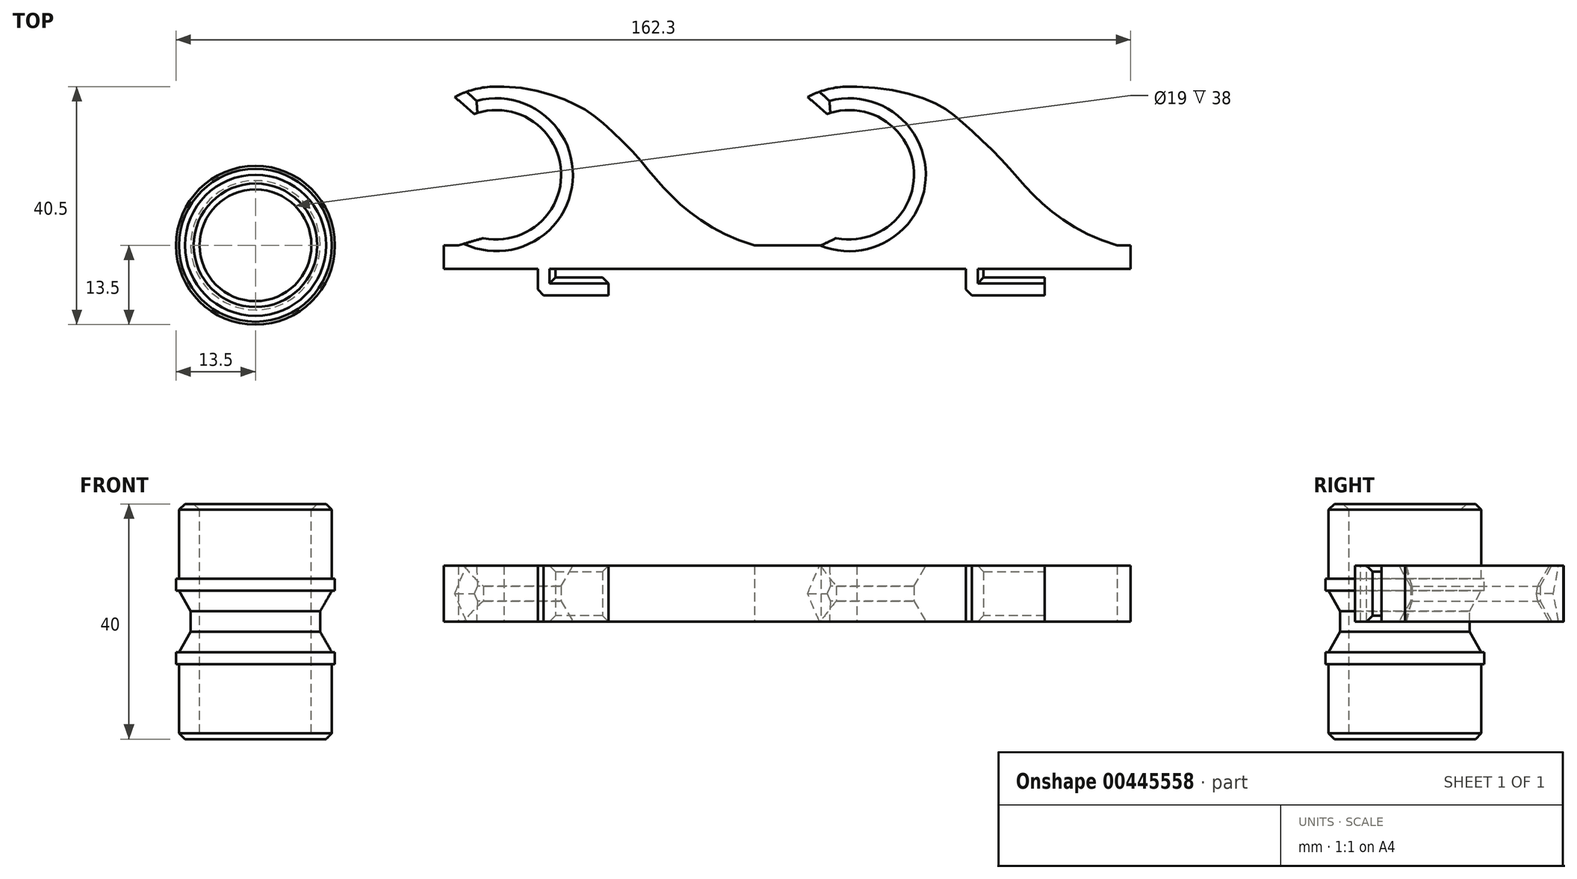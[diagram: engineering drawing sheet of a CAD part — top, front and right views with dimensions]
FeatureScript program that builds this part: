
annotation { "Feature Type Name" : "Feature", "Feature Type Description" : "" }
export const myFeature = defineFeature(function(context is Context, id is Id, definition is map)
    precondition{}
    {
        {
            var Q0;
            Q0=qCreatedBy(makeId("Top.planeOp"),FACE);
            var sketch = newSketch(context, id + "F0", { "sketchPlane" : qUnion([Q0])});
            skLineSegment(sketch, "E0", {"start": v(0, 0) * mm, "end": v(60.8, 0) * mm});
            skLineSegment(sketch, "E1", {"start": v(0, 0) * mm, "end": v(-12, 0) * mm});
            skLineSegment(sketch, "E2", {"start": v(-12, -4) * mm, "end": v(-12, -8.5) * mm});
            skLineSegment(sketch, "E3", {"start": v(-12, -8.5) * mm, "end": v(0, -8.5) * mm});
            skLineSegment(sketch, "E4", {"start": v(0, -8.5) * mm, "end": v(0, -5.5) * mm});
            skLineSegment(sketch, "E5", {"start": v(0, -5.5) * mm, "end": v(-9, -5.5) * mm});
            skLineSegment(sketch, "E6", {"start": v(-9, -5.5) * mm, "end": v(-9, -4) * mm});
            skLineSegment(sketch, "E7", {"start": v(-9, -4) * mm, "end": v(0, -4) * mm});
            skLineSegment(sketch, "E8", {"start": v(60.8, -4) * mm, "end": v(60.8, -8.5) * mm});
            skLineSegment(sketch, "E9", {"start": v(60.8, -8.5) * mm, "end": v(74.2, -8.5) * mm});
            skLineSegment(sketch, "E10", {"start": v(74.2, -8.5) * mm, "end": v(74.2, -5.5) * mm});
            skLineSegment(sketch, "E11", {"start": v(74.2, -5.5) * mm, "end": v(63.8, -5.5) * mm});
            skLineSegment(sketch, "E12", {"start": v(63.8, -5.5) * mm, "end": v(63.8, -4) * mm});
            skLineSegment(sketch, "E13", {"start": v(63.8, -4) * mm, "end": v(74.2, -4) * mm});
            skLineSegment(sketch, "E14", {"start": v(72.8, 0) * mm, "end": v(60.8, 0) * mm});
            skLineSegment(sketch, "E15", {"start": v(-12, 0) * mm, "end": v(-28, 0) * mm});
            skLineSegment(sketch, "E16", {"start": v(88.8, 0) * mm, "end": v(72.8, 0) * mm});
            skLineSegment(sketch, "E17", {"start": v(-28, 0) * mm, "end": v(-28, -4) * mm});
            skLineSegment(sketch, "E18", {"start": v(-28, -4) * mm, "end": v(-12, -4) * mm});
            skLineSegment(sketch, "E19", {"start": v(88.8, 0) * mm, "end": v(88.8, -4) * mm});
            skLineSegment(sketch, "E20", {"start": v(88.8, -4) * mm, "end": v(74.2, -4) * mm});
            skLineSegment(sketch, "E21", {"start": v(0, -4) * mm, "end": v(60.8, -4) * mm});
            skLineSegment(sketch, "E22", {"start": v(24.4, 0) * mm, "end": v(24.4, -4) * mm});
            skSolve(sketch);
        }
        {
            var Q0;
            Q0=qSketchRegion(id+"F0",true);
            extrude(context, id + "F1", {"entities" : qUnion([Q0]), "depth" : 9.5 * mm});
        }
        {
            var Q0;
            Q0=makeQuery(id+"F1.opExtrude","SWEPT_EDGE",EDGE,{"disambiguationData":[OSD([sQuery(id+"F0.wireOp",EDGE,"E2"),sQuery(id+"F0.wireOp",EDGE,"E3")])]});
            var Q1;
            Q1=makeQuery(id+"F1.opExtrude","SWEPT_EDGE",EDGE,{"disambiguationData":[OSD([sQuery(id+"F0.wireOp",EDGE,"E8"),sQuery(id+"F0.wireOp",EDGE,"E9")])]});
            var Q2;
            Q2=makeQuery(id+"F1.opExtrude","SWEPT_EDGE",EDGE,{"disambiguationData":[OSD([sQuery(id+"F0.wireOp",EDGE,"E4"),sQuery(id+"F0.wireOp",EDGE,"E5")])]});
            var Q3;
            Q3=makeQuery(id+"F1.opExtrude","CAP_EDGE",EDGE,{"disambiguationData":[OSD([sQuery(id+"F0.wireOp",EDGE,"E11")])],"isStart":true});
            var Q4;
            Q4=makeQuery(id+"F1.opExtrude","CAP_EDGE",EDGE,{"disambiguationData":[OSD([sQuery(id+"F0.wireOp",EDGE,"E5")])],"isStart":true});
            var Q5;
            Q5=makeQuery(id+"F1.opExtrude","CAP_EDGE",EDGE,{"disambiguationData":[OSD([sQuery(id+"F0.wireOp",EDGE,"E6")])],"isStart":true});
            var Q6;
            Q6=makeQuery(id+"F1.opExtrude","CAP_EDGE",EDGE,{"disambiguationData":[OSD([sQuery(id+"F0.wireOp",EDGE,"E12")])],"isStart":true});
            var Q7;
            Q7=makeQuery(id+"F1.opExtrude","CAP_EDGE",EDGE,{"disambiguationData":[OSD([sQuery(id+"F0.wireOp",EDGE,"E11")])],"isStart":false});
            var Q8;
            Q8=makeQuery(id+"F1.opExtrude","CAP_EDGE",EDGE,{"disambiguationData":[OSD([sQuery(id+"F0.wireOp",EDGE,"E12")])],"isStart":false});
            var Q9;
            Q9=makeQuery(id+"F1.opExtrude","CAP_EDGE",EDGE,{"disambiguationData":[OSD([sQuery(id+"F0.wireOp",EDGE,"E5")])],"isStart":false});
            var Q10;
            Q10=makeQuery(id+"F1.opExtrude","CAP_EDGE",EDGE,{"disambiguationData":[OSD([sQuery(id+"F0.wireOp",EDGE,"E6")])],"isStart":false});
            chamfer(context, id + "F2", {"entities" : qUnion([Q0, Q1, Q2, Q3, Q4, Q5, Q6, Q7, Q8, Q9, Q10]), "width" : 1 * mm, "tangentPropagation" : true});
        }
        {
            var Q0;
            Q0=qCreatedBy(makeId("Top.planeOp"),FACE);
            var sketch = newSketch(context, id + "F3", { "sketchPlane" : qUnion([Q0])});
            skArc(sketch, "E23", {"start": v(38.77, 1.22) * mm, "mid": v(51.01, 16.5) * mm, "end": v(31.47, 17.55) * mm});
            skArc(sketch, "E24", {"start": v(42.27, 26.94) * mm, "mid": v(36.55, 26.33) * mm, "end": v(31.47, 23.6) * mm});
            skLineSegment(sketch, "E25", {"start": v(31.47, 17.55) * mm, "end": v(31.47, 23.6) * mm});
            skLineSegment(sketch, "E26", {"start": v(38.77, 1.22) * mm, "end": v(38.77, 0) * mm});
            skLineSegment(sketch, "E27", {"start": v(38.77, 0) * mm, "end": v(86.52, 0) * mm});
            skLineSegment(sketch, "E28", {"start": v(38.77, 1.22) * mm, "end": v(36.18, 0) * mm});
            skLineSegment(sketch, "E29", {"start": v(36.18, 0) * mm, "end": v(38.77, 0) * mm});
            skFitSpline(sketch, "E30", {"points": [v(42.27, 26.94) * mm, v(55.04, 24.44) * mm, v(60.1, 20.96) * mm, v(66.27, 15.18) * mm, v(71.09, 9.79) * mm, v(76.79, 4.7) * mm, v(86.52, 0) * mm], "startDerivative": vector(69.14, -0.33) * mm, "endDerivative": vector(63.43, -17.78) * mm});
            skArc(sketch, "E31", {"start": v(-21.23, 1.22) * mm, "mid": v(-8.99, 16.5) * mm, "end": v(-28.53, 17.55) * mm});
            skArc(sketch, "E32", {"start": v(-17.73, 26.94) * mm, "mid": v(-23.45, 26.33) * mm, "end": v(-28.53, 23.6) * mm});
            skLineSegment(sketch, "E33", {"start": v(-28.53, 17.55) * mm, "end": v(-28.53, 23.6) * mm});
            skLineSegment(sketch, "E34", {"start": v(-21.23, 1.22) * mm, "end": v(-21.23, 0) * mm});
            skLineSegment(sketch, "E35", {"start": v(-21.23, 0) * mm, "end": v(24.84, 0) * mm});
            skLineSegment(sketch, "E36", {"start": v(-21.23, 1.22) * mm, "end": v(-25.5, 0) * mm});
            skLineSegment(sketch, "E37", {"start": v(-25.5, 0) * mm, "end": v(-21.23, 0) * mm});
            skFitSpline(sketch, "E38", {"points": [v(-17.73, 26.94) * mm, v(-6.64, 24.44) * mm, v(-1.42, 21.22) * mm, v(5.01, 14.92) * mm, v(9.4, 9.79) * mm, v(15.1, 4.7) * mm, v(24.84, 0) * mm], "startDerivative": vector(68.3, -0.33) * mm, "endDerivative": vector(63.43, -17.78) * mm});
            skSolve(sketch);
        }
        {
            var Q0;
            Q0=qSketchRegion(id+"F3",true);
            extrude(context, id + "F4", {"entities" : qUnion([Q0]), "operationType" : NewBodyOperationType.ADD, "depth" : 9.5 * mm});
        }
        {
            var Q0;
            Q0=makeQuery(id+"F4.opExtrude","CAP_EDGE",EDGE,{"disambiguationData":[OSD([sQuery(id+"F3.wireOp",EDGE,"E23")])],"isStart":false});
            var Q1;
            Q1=makeQuery(id+"F4.opExtrude","CAP_EDGE",EDGE,{"disambiguationData":[OSD([sQuery(id+"F3.wireOp",EDGE,"E31")])],"isStart":false});
            chamfer(context, id + "F5", {"entities" : qUnion([Q0, Q1]), "chamferType" : ChamferType.TWO_OFFSETS, "width1" : 3.5 * mm, "oppositeDirection" : false, "width2" : 2 * mm, "tangentPropagation" : true});
        }
        {
            var Q0;
            Q0=makeQuery(id+"F4.opExtrude","CAP_EDGE",EDGE,{"disambiguationData":[OSD([sQuery(id+"F3.wireOp",EDGE,"E31")])],"isStart":true});
            var Q1;
            Q1=makeQuery(id+"F4.opExtrude","CAP_EDGE",EDGE,{"disambiguationData":[OSD([sQuery(id+"F3.wireOp",EDGE,"E23")])],"isStart":true});
            chamfer(context, id + "F6", {"entities" : qUnion([Q0, Q1]), "chamferType" : ChamferType.TWO_OFFSETS, "width1" : 2 * mm, "oppositeDirection" : false, "width2" : 3.5 * mm, "tangentPropagation" : true});
        }
        {
            var Q0;
            Q0=makeQuery(id+"F5.opChamfer","BLEND_EDGE",EDGE,{"blendedFrom":[makeQuery(id+"F4.opExtrude","CAP_EDGE",EDGE,{"disambiguationData":[OSD([sQuery(id+"F3.wireOp",EDGE,"E23")])],"isStart":false}),makeQuery(id+"F4.opExtrude","SWEPT_FACE",FACE,{"disambiguationData":[OSD([sQuery(id+"F3.wireOp",EDGE,"E25")])]})],"blendedInto":[makeQuery(id+"F4.opExtrude","SWEPT_FACE",FACE,{"disambiguationData":[OSD([sQuery(id+"F3.wireOp",EDGE,"E25")])]})]});
            var Q1;
            Q1=makeQuery(id+"F6.opChamfer","BLEND_EDGE",EDGE,{"blendedFrom":[makeQuery(id+"F4.opExtrude","CAP_EDGE",EDGE,{"disambiguationData":[OSD([sQuery(id+"F3.wireOp",EDGE,"E23")])],"isStart":true}),makeQuery(id+"F4.opExtrude","SWEPT_FACE",FACE,{"disambiguationData":[OSD([sQuery(id+"F3.wireOp",EDGE,"E25")])]})],"blendedInto":[makeQuery(id+"F4.opExtrude","SWEPT_FACE",FACE,{"disambiguationData":[OSD([sQuery(id+"F3.wireOp",EDGE,"E25")])]})]});
            var Q2;
            Q2=makeQuery(id+"F5.opChamfer","BLEND_EDGE",EDGE,{"blendedFrom":[makeQuery(id+"F4.opExtrude","CAP_EDGE",EDGE,{"disambiguationData":[OSD([sQuery(id+"F3.wireOp",EDGE,"E31")])],"isStart":false}),makeQuery(id+"F4.opExtrude","SWEPT_FACE",FACE,{"disambiguationData":[OSD([sQuery(id+"F3.wireOp",EDGE,"E33")])]})],"blendedInto":[makeQuery(id+"F4.opExtrude","SWEPT_FACE",FACE,{"disambiguationData":[OSD([sQuery(id+"F3.wireOp",EDGE,"E33")])]})]});
            var Q3;
            Q3=makeQuery(id+"F6.opChamfer","BLEND_EDGE",EDGE,{"blendedFrom":[makeQuery(id+"F4.opExtrude","CAP_EDGE",EDGE,{"disambiguationData":[OSD([sQuery(id+"F3.wireOp",EDGE,"E31")])],"isStart":true}),makeQuery(id+"F4.opExtrude","SWEPT_FACE",FACE,{"disambiguationData":[OSD([sQuery(id+"F3.wireOp",EDGE,"E33")])]})],"blendedInto":[makeQuery(id+"F4.opExtrude","SWEPT_FACE",FACE,{"disambiguationData":[OSD([sQuery(id+"F3.wireOp",EDGE,"E33")])]})]});
            chamfer(context, id + "F7", {"entities" : qUnion([Q0, Q1, Q2, Q3]), "width" : 5 * mm, "tangentPropagation" : true});
        }
        {
            var Q0;
            Q0=qCreatedBy(makeId("Front.planeOp"),FACE);
            var sketch = newSketch(context, id + "F8", { "sketchPlane" : qUnion([Q0])});
            skLineSegment(sketch, "E39", {"start": v(0, 0) * mm, "end": v(-60, 0) * mm});
            skLineSegment(sketch, "E40", {"start": v(-60, 0) * mm, "end": v(-60, -12.67) * mm});
            skLineSegment(sketch, "E41", {"start": v(-60, 0) * mm, "end": v(-69.5, 0) * mm});
            skLineSegment(sketch, "E42", {"start": v(-69.5, 0) * mm, "end": v(-73, 0) * mm});
            skLineSegment(sketch, "E43", {"start": v(-69.5, 0) * mm, "end": v(-69.5, 20) * mm});
            skLineSegment(sketch, "E44", {"start": v(-69.5, 20) * mm, "end": v(-73, 20) * mm});
            skLineSegment(sketch, "E45", {"start": v(-73, 20) * mm, "end": v(-73, 5.25) * mm});
            skLineSegment(sketch, "E46", {"start": v(-73, 5.25) * mm, "end": v(-71, 1.75) * mm});
            skLineSegment(sketch, "E47", {"start": v(-71, 1.75) * mm, "end": v(-71, 0) * mm});
            skLineSegment(sketch, "E48.MirrorCS", {"start": v(-71, -1.75) * mm, "end": v(-71, 0) * mm});
            skLineSegment(sketch, "E49.MirrorCS", {"start": v(-73, -5.25) * mm, "end": v(-71, -1.75) * mm});
            skLineSegment(sketch, "E50.MirrorCS", {"start": v(-73, -20) * mm, "end": v(-73, -5.25) * mm});
            skLineSegment(sketch, "E51.MirrorCS", {"start": v(-69.5, -20) * mm, "end": v(-73, -20) * mm});
            skLineSegment(sketch, "E52.MirrorCS", {"start": v(-69.5, 0) * mm, "end": v(-69.5, -20) * mm});
            skLineSegment(sketch, "E53", {"start": v(-73, 5.25) * mm, "end": v(-73.5, 5.25) * mm});
            skLineSegment(sketch, "E54", {"start": v(-73.5, 5.25) * mm, "end": v(-73.5, 7.25) * mm});
            skLineSegment(sketch, "E55", {"start": v(-73.5, 7.25) * mm, "end": v(-73, 7.25) * mm});
            skLineSegment(sketch, "E56.MirrorCS", {"start": v(-73.5, -7.25) * mm, "end": v(-73, -7.25) * mm});
            skLineSegment(sketch, "E57.MirrorCS", {"start": v(-73.5, -5.25) * mm, "end": v(-73.5, -7.25) * mm});
            skLineSegment(sketch, "E58.MirrorCS", {"start": v(-73, -5.25) * mm, "end": v(-73.5, -5.25) * mm});
            skSolve(sketch);
        }
        {
            var Q0;
            Q0=qSketchRegion(id+"F8",true);
            var Q1;
            Q1=sQuery(id+"F8.wireOp",EDGE,"E40");
            revolve(context, id + "F9", {"entities" : qUnion([Q0]), "axis" : qUnion([Q1]), "revolveType" : RevolveType.FULL});
        }
        {
            var Q0;
            Q0=makeQuery(id+"F9.opRevolve","SWEPT_FACE",FACE,{"disambiguationData":[OSD([sQuery(id+"F8.wireOp",EDGE,"E51.MirrorCS")])]});
            var sketch = newSketch(context, id + "F10", { "sketchPlane" : qUnion([Q0])});
            skCircle(sketch, "E59", {"center": v(-60, 0) * mm, "radius": 13 * mm});
            skSolve(sketch);
        }
        {
            var Q0;
            Q0=qSketchRegion(id+"F10",true);
            extrude(context, id + "F11", {"entities" : qUnion([Q0]), "operationType" : NewBodyOperationType.ADD, "oppositeDirection" : true, "depth" : 1 * mm});
        }
        {
            var Q0;
            Q0=makeQuery(id+"F9.opRevolve","SWEPT_EDGE",EDGE,{"disambiguationData":[OSD([sQuery(id+"F8.wireOp",EDGE,"E50.MirrorCS"),sQuery(id+"F8.wireOp",EDGE,"E51.MirrorCS")])]});
            var Q1;
            Q1=makeQuery(id+"F9.opRevolve","SWEPT_FACE",FACE,{"disambiguationData":[OSD([sQuery(id+"F8.wireOp",EDGE,"E44")])]});
            chamfer(context, id + "F12", {"entities" : qUnion([Q0, Q1]), "width" : 1 * mm, "tangentPropagation" : true});
        }
    });
